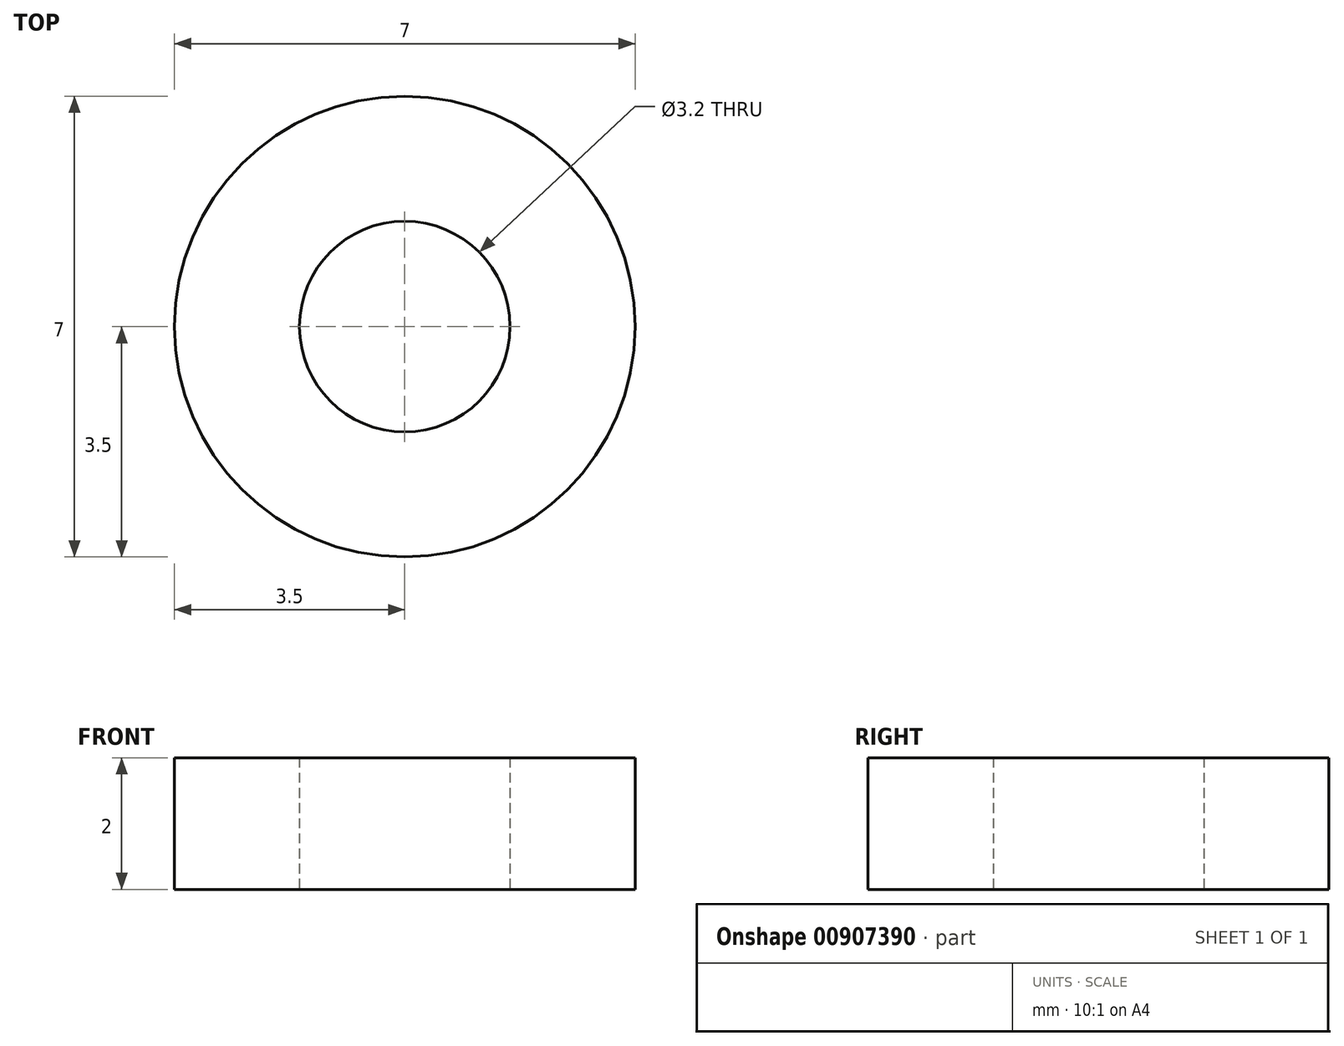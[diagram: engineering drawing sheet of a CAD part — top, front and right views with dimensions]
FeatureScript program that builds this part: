
annotation { "Feature Type Name" : "Feature", "Feature Type Description" : "" }
export const myFeature = defineFeature(function(context is Context, id is Id, definition is map)
    precondition{}
    {
        {
            var Q0;
            Q0=qCreatedBy(makeId("Top.planeOp"),FACE);
            var sketch = newSketch(context, id + "F0", { "sketchPlane" : qUnion([Q0])});
            skCircle(sketch, "E0", {"center": v(0, 0) * mm, "radius": 3.5 * mm});
            skCircle(sketch, "E1", {"center": v(0, 0) * mm, "radius": 1.6 * mm});
            skSolve(sketch);
        }
        {
            var Q0;
            Q0=makeQuery(id+"F0.imprint","IMPRINT",FACE,{"disambiguationData":[TD([[makeQuery(id+"F0.imprint","IMPRINT",EDGE,{"derivedFrom":sQuery(id+"F0.wireOp",EDGE,"E0")}),1.0]])]});
            extrude(context, id + "F1", {"entities" : qUnion([Q0]), "depth" : 2 * mm, "offsetDistance" : 25 * mm});
        }
    });
